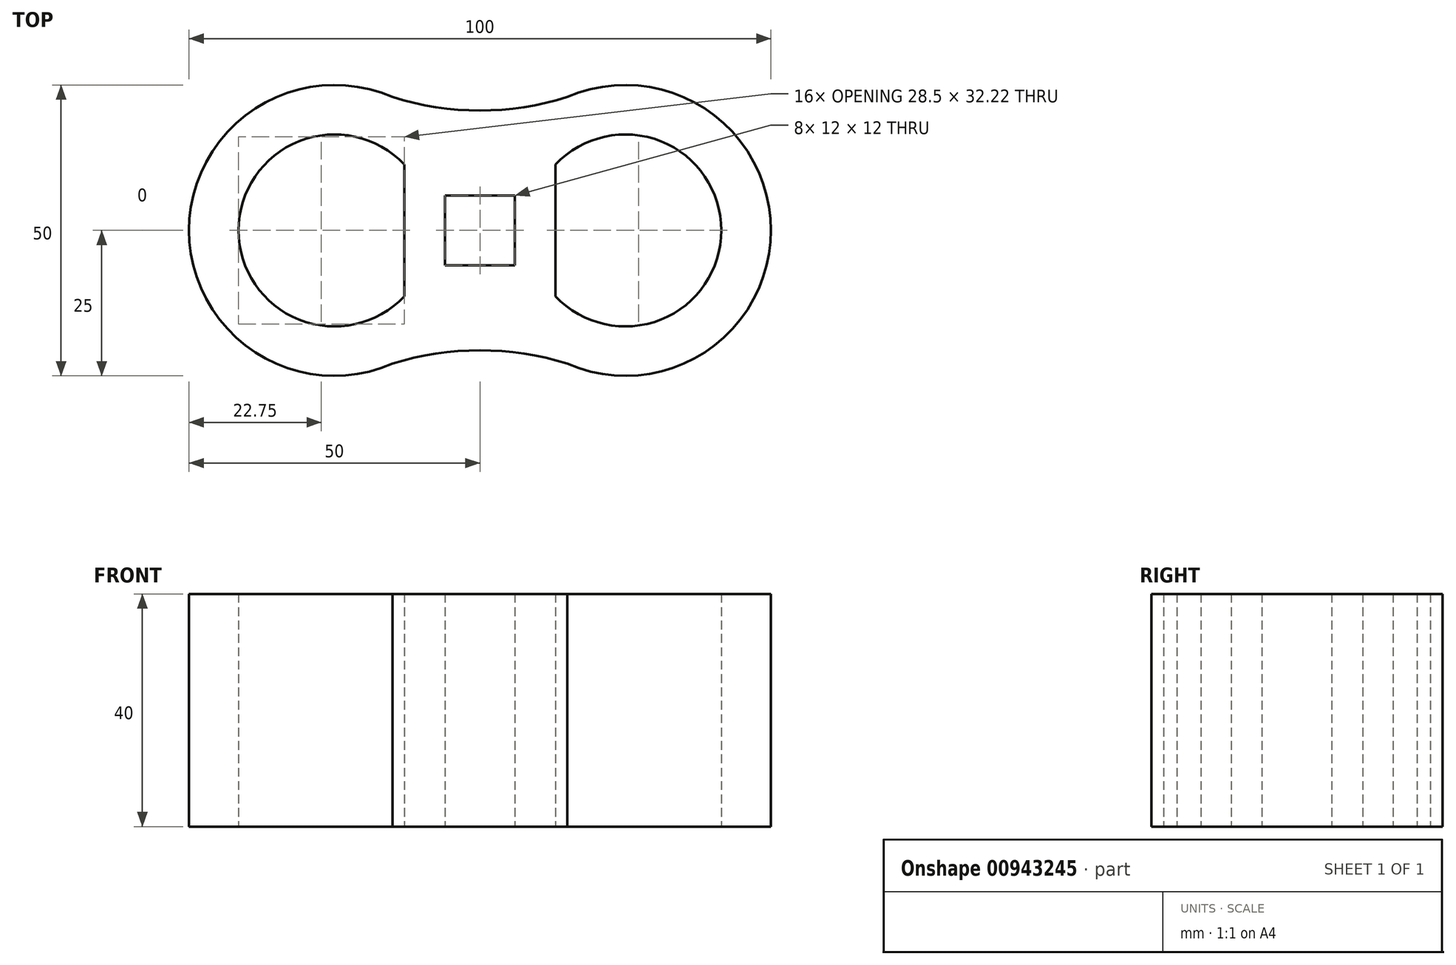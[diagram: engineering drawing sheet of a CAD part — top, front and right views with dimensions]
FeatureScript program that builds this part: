
annotation { "Feature Type Name" : "Feature", "Feature Type Description" : "" }
export const myFeature = defineFeature(function(context is Context, id is Id, definition is map)
    precondition{}
    {
        {
            var Q0;
            Q0=qCreatedBy(makeId("Top.planeOp"),FACE);
            var sketch = newSketch(context, id + "F0", { "sketchPlane" : qUnion([Q0])});
            skLineSegment(sketch, "E0.bottom", {"start": v(6, -6) * mm, "end": v(-6, -6) * mm});
            skLineSegment(sketch, "E0.top", {"start": v(6, 6) * mm, "end": v(-6, 6) * mm});
            skLineSegment(sketch, "E0.left", {"start": v(6, -6) * mm, "end": v(6, 6) * mm});
            skLineSegment(sketch, "E0.right", {"start": v(-6, -6) * mm, "end": v(-6, 6) * mm});
            skPoint(sketch, "E0.middle", {"position": v(0, 0) * mm});
            skArc(sketch, "E1", {"start": v(-15.02, 22.92) * mm, "mid": v(-50, 0) * mm, "end": v(-15.02, -22.92) * mm});
            skArc(sketch, "E2", {"start": v(-13, 11.32) * mm, "mid": v(-41.5, 0) * mm, "end": v(-13, -11.32) * mm});
            skArc(sketch, "E3.MirrorC", {"start": v(13, 11.32) * mm, "mid": v(41.5, 0) * mm, "end": v(13, -11.32) * mm});
            skArc(sketch, "E4.MirrorC", {"start": v(15.02, 22.92) * mm, "mid": v(50, 0) * mm, "end": v(15.02, -22.92) * mm});
            skArc(sketch, "E5", {"start": v(-18.34, 24.1) * mm, "mid": v(0, 20.61) * mm, "end": v(18.34, 24.1) * mm});
            skArc(sketch, "E6.MirrorCS", {"start": v(-18.34, -24.1) * mm, "mid": v(0, -20.61) * mm, "end": v(18.34, -24.1) * mm});
            skLineSegment(sketch, "E7", {"start": v(-13, -11.32) * mm, "end": v(-13, 11.32) * mm});
            skLineSegment(sketch, "E8.MirrorCS", {"start": v(13, -11.32) * mm, "end": v(13, 11.32) * mm});
            skPoint(sketch, "E9.orphan", {"position": v(-13, 0) * mm});
            skSolve(sketch);
        }
        {
            var Q0;
            Q0=qSketchRegion(id+"F0",true);
            extrude(context, id + "F1", {"entities" : qUnion([Q0]), "depth" : 40 * mm});
        }
    });
